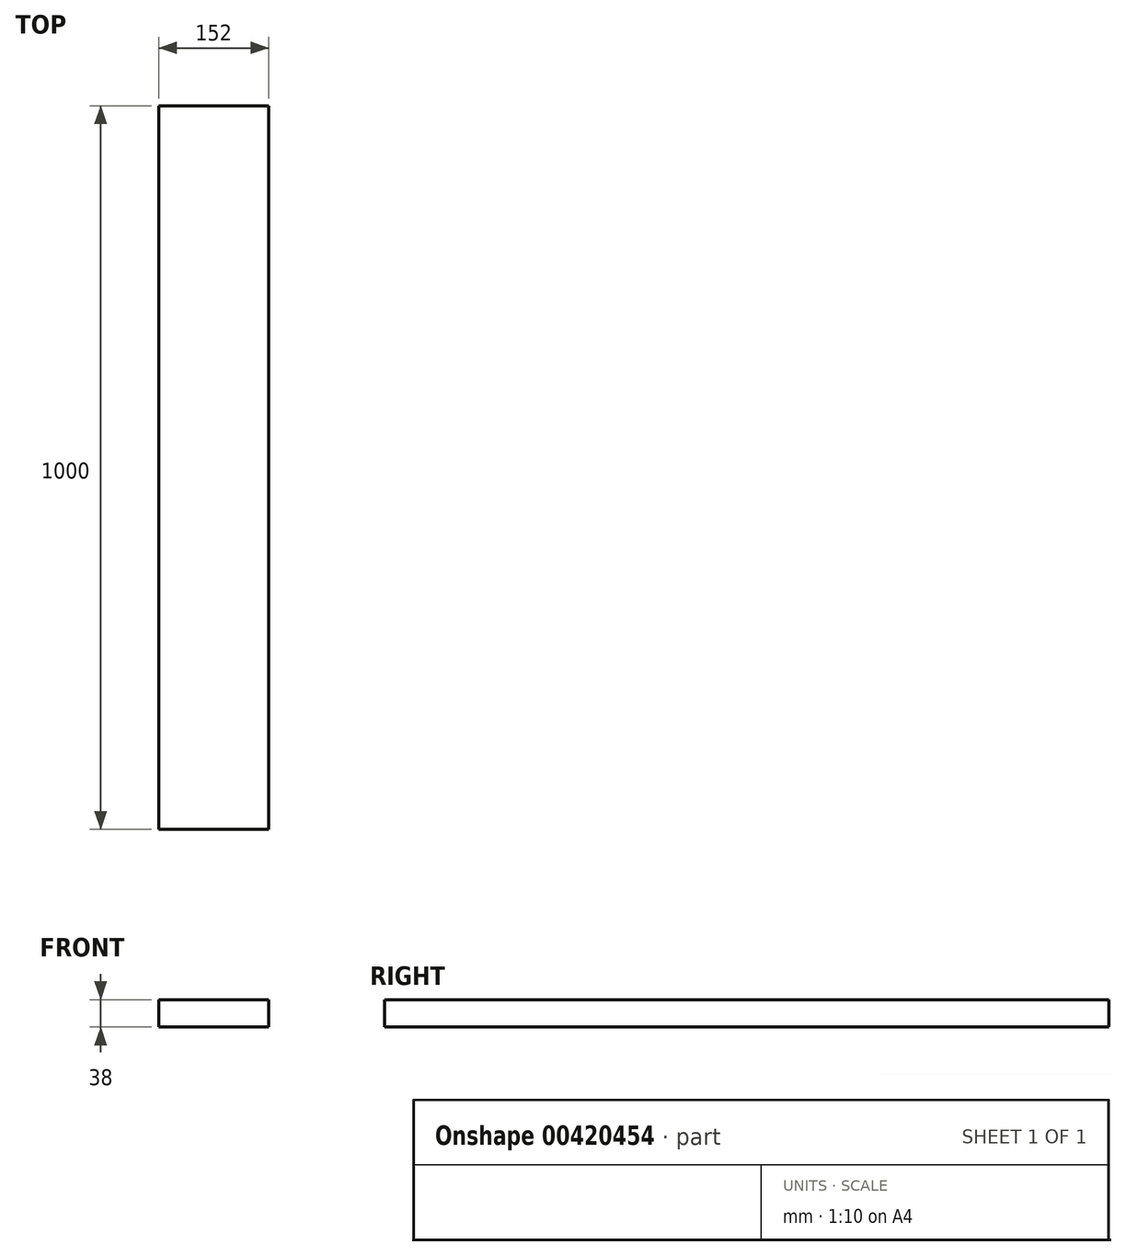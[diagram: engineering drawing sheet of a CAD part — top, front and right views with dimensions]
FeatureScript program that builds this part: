
annotation { "Feature Type Name" : "Feature", "Feature Type Description" : "" }
export const myFeature = defineFeature(function(context is Context, id is Id, definition is map)
    precondition{}
    {
        {
            var Q0;
            Q0=qCreatedBy(makeId("Front.planeOp"),FACE);
            var sketch = newSketch(context, id + "F0", { "sketchPlane" : qUnion([Q0])});
            skLineSegment(sketch, "E0.bottom", {"start": v(76, 19) * mm, "end": v(-76, 19) * mm});
            skLineSegment(sketch, "E0.top", {"start": v(76, -19) * mm, "end": v(-76, -19) * mm});
            skLineSegment(sketch, "E0.left", {"start": v(76, 19) * mm, "end": v(76, -19) * mm});
            skLineSegment(sketch, "E0.right", {"start": v(-76, 19) * mm, "end": v(-76, -19) * mm});
            skPoint(sketch, "E0.middle", {"position": v(0, 0) * mm});
            skSolve(sketch);
        }
        {
            var Q0;
            Q0=makeQuery(id+"F0.imprint","IMPRINT",FACE,{"disambiguationData":[TD([[makeQuery(id+"F0.imprint","IMPRINT",EDGE,{"derivedFrom":sQuery(id+"F0.wireOp",EDGE,"E0.bottom")}),1.0]])]});
            extrude(context, id + "F1", {"entities" : qUnion([Q0]), "endBound" : BoundingType.SYMMETRIC, "depth" : 1000 * mm});
        }
    });
